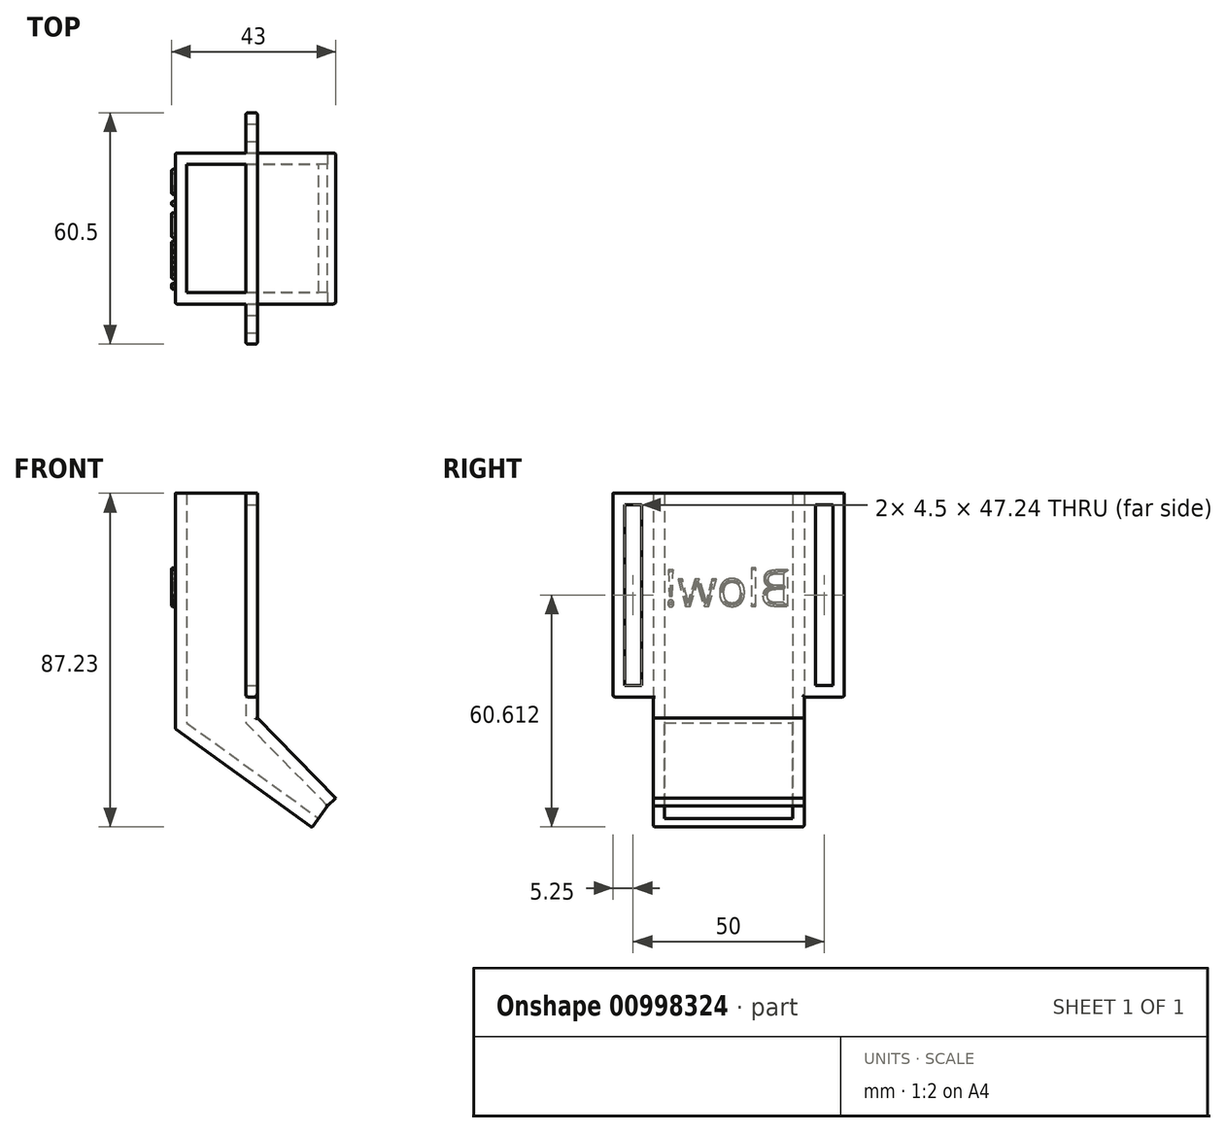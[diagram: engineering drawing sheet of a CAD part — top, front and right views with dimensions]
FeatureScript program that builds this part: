
annotation { "Feature Type Name" : "Feature", "Feature Type Description" : "" }
export const myFeature = defineFeature(function(context is Context, id is Id, definition is map)
    precondition{}
    {
        {
            assignVariable(context, id + "F0", {"name" : "lenght", "anyValue" : 33.5});
        }
        {
            assignVariable(context, id + "F1", {"name" : "WallThicness", "anyValue" : 3});
        }
        {
            assignVariable(context, id + "F2", {"name" : "screwdiam", "anyValue" : 4.5});
        }
        {
            var Q0;
            Q0=qCreatedBy(makeId("Front.planeOp"),FACE);
            var sketch = newSketch(context, id + "F3", { "sketchPlane" : qUnion([Q0])});
            skLineSegment(sketch, "E0.bottom", {"start": v(-2.56, 51.75) * mm, "end": v(12.94, 51.75) * mm});
            skLineSegment(sketch, "E0.left", {"start": v(-2.56, 51.75) * mm, "end": v(-2.56, -8.25) * mm});
            skLineSegment(sketch, "E0.right", {"start": v(12.94, 51.75) * mm, "end": v(12.94, -8.25) * mm});
            skLineSegment(sketch, "E1", {"start": v(-2.56, -8.25) * mm, "end": v(31.95, -33.25) * mm});
            skLineSegment(sketch, "E2", {"start": v(31.95, -33.25) * mm, "end": v(34.3, -30) * mm});
            skLineSegment(sketch, "E3", {"start": v(34.3, -30) * mm, "end": v(12.94, -8.25) * mm});
            skLineSegment(sketch, "E4.0", {"start": v(36.44, -27.9) * mm, "end": v(15.94, -7.02) * mm});
            skLineSegment(sketch, "E4.1", {"start": v(15.94, 51.75) * mm, "end": v(15.94, -7.02) * mm});
            skLineSegment(sketch, "E5.0", {"start": v(-5.56, -9.78) * mm, "end": v(30.19, -35.68) * mm});
            skLineSegment(sketch, "E5.1", {"start": v(-5.56, 51.75) * mm, "end": v(-5.56, -9.78) * mm});
            skLineSegment(sketch, "E6", {"start": v(12.94, 51.75) * mm, "end": v(15.94, 51.75) * mm});
            skLineSegment(sketch, "E7", {"start": v(-5.56, 51.75) * mm, "end": v(-2.56, 51.75) * mm});
            skLineSegment(sketch, "E8", {"start": v(31.95, -33.25) * mm, "end": v(30.19, -35.68) * mm});
            skLineSegment(sketch, "E9", {"start": v(36.44, -27.9) * mm, "end": v(34.3, -30) * mm});
            skSolve(sketch);
        }
        {
            var Q0;
            Q0=makeQuery(id+"F3.imprint","IMPRINT",FACE,{"disambiguationData":[TD([[makeQuery(id+"F3.imprint","IMPRINT",EDGE,{"derivedFrom":sQuery(id+"F3.wireOp",EDGE,"E0.right")}),1.0]])]});
            var Q1;
            Q1=makeQuery(id+"F3.imprint","IMPRINT",FACE,{"disambiguationData":[TD([[makeQuery(id+"F3.imprint","IMPRINT",EDGE,{"derivedFrom":sQuery(id+"F3.wireOp",EDGE,"E0.left")}),-1.0]])]});
            extrude(context, id + "F4", {"entities" : qUnion([Q0, Q1]), "endBound" : BoundingType.SYMMETRIC, "depth" : (getVariable(context, 'lenght')) * mm, "offsetDistance" : 25 * mm});
        }
        {
            var Q0;
            Q0 = qSketchRegion(id + "F3", true);
            extrude(context, id + "F5", {"entities" : qUnion([Q0]), "endBound" : BoundingType.SYMMETRIC, "oppositeDirection" : true, "depth" : (getVariable(context, 'WallThicness')) * mm, "offsetDistance" : 25 * mm});
        }
        {
            var Q0;
            Q0=makeQuery(id+"F5.opExtrude","SWEPT_BODY",BODY,{"disambiguationData":[OSD([sQuery(id+"F3.wireOp",EDGE,"E0.bottom"),sQuery(id+"F3.wireOp",EDGE,"E2"),sQuery(id+"F3.wireOp",EDGE,"E4.0"),sQuery(id+"F3.wireOp",EDGE,"E4.1"),sQuery(id+"F3.wireOp",EDGE,"E5.0"),sQuery(id+"F3.wireOp",EDGE,"E5.1"),sQuery(id+"F3.wireOp",EDGE,"E6"),sQuery(id+"F3.wireOp",EDGE,"E7"),sQuery(id+"F3.wireOp",EDGE,"E8"),sQuery(id+"F3.wireOp",EDGE,"E9")])]});
            var Q1;
            Q1=makeQuery(id+"F4.opExtrude","SWEPT_EDGE",EDGE,{"disambiguationData":[OSD([sQuery(id+"F3.wireOp",EDGE,"E5.1"),sQuery(id+"F3.wireOp",EDGE,"E7")])]});
            transform(context, id + "F6", {"entities" : qUnion([Q0]), "transformType" : TransformType.TRANSLATION_DISTANCE, "transformDirection" : qUnion([Q1]), "distance" : ((getVariable(context, 'lenght') + getVariable(context, 'WallThicness')) / 2) * mm, "oppositeDirection" : true, "makeCopy" : true});
        }
        {
            var Q0;
            Q0=makeQuery(id+"F5.opExtrude","SWEPT_BODY",BODY,{"disambiguationData":[OSD([sQuery(id+"F3.wireOp",EDGE,"E0.bottom"),sQuery(id+"F3.wireOp",EDGE,"E2"),sQuery(id+"F3.wireOp",EDGE,"E4.0"),sQuery(id+"F3.wireOp",EDGE,"E4.1"),sQuery(id+"F3.wireOp",EDGE,"E5.0"),sQuery(id+"F3.wireOp",EDGE,"E5.1"),sQuery(id+"F3.wireOp",EDGE,"E6"),sQuery(id+"F3.wireOp",EDGE,"E7"),sQuery(id+"F3.wireOp",EDGE,"E8"),sQuery(id+"F3.wireOp",EDGE,"E9")])]});
            var Q1;
            Q1=makeQuery(id+"F4.opExtrude","SWEPT_EDGE",EDGE,{"disambiguationData":[OSD([sQuery(id+"F3.wireOp",EDGE,"E5.1"),sQuery(id+"F3.wireOp",EDGE,"E7")])]});
            transform(context, id + "F7", {"entities" : qUnion([Q0]), "transformType" : TransformType.TRANSLATION_DISTANCE, "transformDirection" : qUnion([Q1]), "distance" : ((getVariable(context, 'lenght') + getVariable(context, 'WallThicness')) / 2) * mm, "makeCopy" : false});
        }
        {
            var Q0;
            Q0=makeQuery(id+"F5.opExtrude","CAP_FACE",FACE,{"disambiguationData":[OSD([sQuery(id+"F3.wireOp",EDGE,"E0.bottom"),sQuery(id+"F3.wireOp",EDGE,"E2"),sQuery(id+"F3.wireOp",EDGE,"E4.0"),sQuery(id+"F3.wireOp",EDGE,"E4.1"),sQuery(id+"F3.wireOp",EDGE,"E5.0"),sQuery(id+"F3.wireOp",EDGE,"E5.1"),sQuery(id+"F3.wireOp",EDGE,"E6"),sQuery(id+"F3.wireOp",EDGE,"E7"),sQuery(id+"F3.wireOp",EDGE,"E8"),sQuery(id+"F3.wireOp",EDGE,"E9")])],"isStart":true});
            var sketch = newSketch(context, id + "F8", { "sketchPlane" : qUnion([Q0])});
            skLineSegment(sketch, "E10.bottom", {"start": v(15.94, 51.75) * mm, "end": v(12.94, 51.75) * mm});
            skLineSegment(sketch, "E10.top", {"start": v(15.94, -1.49) * mm, "end": v(12.94, -1.49) * mm});
            skLineSegment(sketch, "E10.left", {"start": v(15.94, 51.75) * mm, "end": v(15.94, -1.49) * mm});
            skLineSegment(sketch, "E10.right", {"start": v(12.94, 51.75) * mm, "end": v(12.94, -1.49) * mm});
            skSolve(sketch);
        }
        {
            var Q0;
            Q0 = qSketchRegion(id + "F8", true);
            extrude(context, id + "F9", {"entities" : qUnion([Q0]), "oppositeDirection" : true, "depth" : (3 * getVariable(context, 'WallThicness') + getVariable(context, 'screwdiam')) * mm, "offsetDistance" : 25 * mm});
        }
        {
            var Q0;
            Q0=makeQuery(id+"F9.opExtrude","SWEPT_FACE",FACE,{"disambiguationData":[OSD([sQuery(id+"F8.wireOp",EDGE,"E10.left")])]});
            var sketch = newSketch(context, id + "F10", { "sketchPlane" : qUnion([Q0])});
            skLineSegment(sketch, "E11.bottom", {"start": v(27.25, 48.75) * mm, "end": v(22.75, 48.75) * mm});
            skLineSegment(sketch, "E11.top", {"start": v(27.25, 1.51) * mm, "end": v(22.75, 1.51) * mm});
            skLineSegment(sketch, "E11.left", {"start": v(27.25, 48.75) * mm, "end": v(27.25, 1.51) * mm});
            skLineSegment(sketch, "E11.right", {"start": v(22.75, 48.75) * mm, "end": v(22.75, 1.51) * mm});
            skSolve(sketch);
        }
        {
            var Q0;
            Q0=makeQuery(id+"F10.imprint","IMPRINT",FACE,{"disambiguationData":[TD([[makeQuery(id+"F10.imprint","IMPRINT",EDGE,{"derivedFrom":sQuery(id+"F10.wireOp",EDGE,"E11.bottom")}),1.0]])]});
            extrude(context, id + "F11", {"entities" : qUnion([Q0]), "operationType" : NewBodyOperationType.REMOVE, "endBound" : BoundingType.THROUGH_ALL, "oppositeDirection" : true, "depth" : 25 * mm, "offsetDistance" : 25 * mm});
        }
        {
            var Q0;
            Q0=makeQuery(id+"F9.opExtrude","SWEPT_BODY",BODY,{"disambiguationData":[OSD([sQuery(id+"F8.wireOp",EDGE,"E10.bottom"),sQuery(id+"F8.wireOp",EDGE,"E10.top"),sQuery(id+"F8.wireOp",EDGE,"E10.left"),sQuery(id+"F8.wireOp",EDGE,"E10.right")])]});
            var Q1;
            Q1=qCreatedBy(makeId("Front.planeOp"),FACE);
            mirror(context, id + "F12", {"operationType" : NewBodyOperationType.ADD, "entities" : qUnion([Q0]), "mirrorPlane" : qUnion([Q1])});
        }
        {
            var Q0;
            Q0=makeQuery(id+"F4.opExtrude","SWEPT_BODY",BODY,{"disambiguationData":[OSD([sQuery(id+"F3.wireOp",EDGE,"E0.left"),sQuery(id+"F3.wireOp",EDGE,"E1"),sQuery(id+"F3.wireOp",EDGE,"E5.0"),sQuery(id+"F3.wireOp",EDGE,"E5.1"),sQuery(id+"F3.wireOp",EDGE,"E7"),sQuery(id+"F3.wireOp",EDGE,"E8")])]});
            var Q1;
            Q1=makeQuery(id+"F4.opExtrude","SWEPT_BODY",BODY,{"disambiguationData":[OSD([sQuery(id+"F3.wireOp",EDGE,"E0.right"),sQuery(id+"F3.wireOp",EDGE,"E3"),sQuery(id+"F3.wireOp",EDGE,"E4.0"),sQuery(id+"F3.wireOp",EDGE,"E4.1"),sQuery(id+"F3.wireOp",EDGE,"E6"),sQuery(id+"F3.wireOp",EDGE,"E9")])]});
            var Q2;
            Q2=makeQuery(id+"F5.opExtrude","SWEPT_BODY",BODY,{"disambiguationData":[OSD([sQuery(id+"F3.wireOp",EDGE,"E0.bottom"),sQuery(id+"F3.wireOp",EDGE,"E2"),sQuery(id+"F3.wireOp",EDGE,"E4.0"),sQuery(id+"F3.wireOp",EDGE,"E4.1"),sQuery(id+"F3.wireOp",EDGE,"E5.0"),sQuery(id+"F3.wireOp",EDGE,"E5.1"),sQuery(id+"F3.wireOp",EDGE,"E6"),sQuery(id+"F3.wireOp",EDGE,"E7"),sQuery(id+"F3.wireOp",EDGE,"E8"),sQuery(id+"F3.wireOp",EDGE,"E9")])]});
            var Q3;
            Q3=makeQuery(id+"F6.opPattern","COPY",BODY,{"derivedFrom":makeQuery(id+"F5.opExtrude","SWEPT_BODY",BODY,{"disambiguationData":[OSD([sQuery(id+"F3.wireOp",EDGE,"E0.bottom"),sQuery(id+"F3.wireOp",EDGE,"E2"),sQuery(id+"F3.wireOp",EDGE,"E4.0"),sQuery(id+"F3.wireOp",EDGE,"E4.1"),sQuery(id+"F3.wireOp",EDGE,"E5.0"),sQuery(id+"F3.wireOp",EDGE,"E5.1"),sQuery(id+"F3.wireOp",EDGE,"E6"),sQuery(id+"F3.wireOp",EDGE,"E7"),sQuery(id+"F3.wireOp",EDGE,"E8"),sQuery(id+"F3.wireOp",EDGE,"E9")])]}),"instanceName":"1"});
            var Q4;
            Q4=makeQuery(id+"F9.opExtrude","SWEPT_BODY",BODY,{"disambiguationData":[OSD([sQuery(id+"F8.wireOp",EDGE,"E10.bottom"),sQuery(id+"F8.wireOp",EDGE,"E10.top"),sQuery(id+"F8.wireOp",EDGE,"E10.left"),sQuery(id+"F8.wireOp",EDGE,"E10.right")])]});
            var Q5;
            Q5=makeQuery(id+"F12.opPattern","COPY",BODY,{"derivedFrom":makeQuery(id+"F9.opExtrude","SWEPT_BODY",BODY,{"disambiguationData":[OSD([sQuery(id+"F8.wireOp",EDGE,"E10.bottom"),sQuery(id+"F8.wireOp",EDGE,"E10.top"),sQuery(id+"F8.wireOp",EDGE,"E10.left"),sQuery(id+"F8.wireOp",EDGE,"E10.right")])]}),"instanceName":"1"});
            booleanBodies(context, id + "F13", {"operationType" : BooleanOperationType.UNION, "tools" : qUnion([Q0, Q1, Q2, Q3, Q4, Q5])});
        }
        {
            var Q0;
            {var subQ0=sQuery(id+"F3.wireOp",EDGE,"E9");var subQ1=sQuery(id+"F3.wireOp",EDGE,"E4.0");var subQ2=makeQuery(id+"F5.opExtrude","SWEPT_EDGE",EDGE,{"disambiguationData":[OSD([subQ1,subQ0])]});Q0=makeQuery(id+"F13.opBoolean","MERGE",EDGE,{"derivedFrom":[makeQuery(id+"F4.opExtrude","SWEPT_EDGE",EDGE,{"disambiguationData":[OSD([subQ1,subQ0])]}),subQ2,makeQuery(id+"F6.opPattern","COPY",EDGE,{"derivedFrom":subQ2,"instanceName":"1"})]});}
            var Q1;
            Q1=makeQuery(id+"F5.opExtrude","CAP_EDGE",EDGE,{"disambiguationData":[OSD([sQuery(id+"F3.wireOp",EDGE,"E4.0")])],"isStart":false});
            var Q2;
            Q2=makeQuery(id+"F5.opExtrude","CAP_EDGE",EDGE,{"disambiguationData":[OSD([sQuery(id+"F3.wireOp",EDGE,"E2"),sQuery(id+"F3.wireOp",EDGE,"E8")])],"isStart":false});
            var Q3;
            Q3=makeQuery(id+"F5.opExtrude","CAP_EDGE",EDGE,{"disambiguationData":[OSD([sQuery(id+"F3.wireOp",EDGE,"E9")])],"isStart":false});
            var Q4;
            {var subQ0=sQuery(id+"F3.wireOp",EDGE,"E8");var subQ1=sQuery(id+"F3.wireOp",EDGE,"E5.0");var subQ2=makeQuery(id+"F5.opExtrude","SWEPT_EDGE",EDGE,{"disambiguationData":[OSD([subQ1,subQ0])]});Q4=makeQuery(id+"F13.opBoolean","MERGE",EDGE,{"derivedFrom":[makeQuery(id+"F4.opExtrude","SWEPT_EDGE",EDGE,{"disambiguationData":[OSD([subQ1,subQ0])]}),subQ2,makeQuery(id+"F6.opPattern","COPY",EDGE,{"derivedFrom":subQ2,"instanceName":"1"})]});}
            var Q5;
            Q5=makeQuery(id+"F6.opPattern","COPY",EDGE,{"derivedFrom":makeQuery(id+"F5.opExtrude","CAP_EDGE",EDGE,{"disambiguationData":[OSD([sQuery(id+"F3.wireOp",EDGE,"E9")])],"isStart":true}),"instanceName":"1"});
            var Q6;
            Q6=makeQuery(id+"F6.opPattern","COPY",EDGE,{"derivedFrom":makeQuery(id+"F5.opExtrude","CAP_EDGE",EDGE,{"disambiguationData":[OSD([sQuery(id+"F3.wireOp",EDGE,"E2"),sQuery(id+"F3.wireOp",EDGE,"E8")])],"isStart":true}),"instanceName":"1"});
            var Q7;
            Q7=makeQuery(id+"F6.opPattern","COPY",EDGE,{"derivedFrom":makeQuery(id+"F5.opExtrude","CAP_EDGE",EDGE,{"disambiguationData":[OSD([sQuery(id+"F3.wireOp",EDGE,"E4.0")])],"isStart":true}),"instanceName":"1"});
            var Q8;
            Q8=makeQuery(id+"F5.opExtrude","CAP_EDGE",EDGE,{"disambiguationData":[OSD([sQuery(id+"F3.wireOp",EDGE,"E4.1")])],"isStart":false});
            var Q9;
            Q9=makeQuery(id+"F9.opExtrude","SWEPT_EDGE",EDGE,{"disambiguationData":[OSD([sQuery(id+"F3.wireOp",EDGE,"E4.1"),sQuery(id+"F8.wireOp",EDGE,"E10.top"),sQuery(id+"F8.wireOp",EDGE,"E10.left")])]});
            var Q10;
            Q10=makeQuery(id+"F9.opExtrude","CAP_EDGE",EDGE,{"disambiguationData":[OSD([sQuery(id+"F8.wireOp",EDGE,"E10.left")])],"isStart":false});
            var Q11;
            Q11=makeQuery(id+"F5.opExtrude","CAP_EDGE",EDGE,{"disambiguationData":[OSD([sQuery(id+"F3.wireOp",EDGE,"E5.0")])],"isStart":false});
            var Q12;
            Q12=makeQuery(id+"F5.opExtrude","CAP_EDGE",EDGE,{"disambiguationData":[OSD([sQuery(id+"F3.wireOp",EDGE,"E5.1")])],"isStart":false});
            var Q13;
            Q13=makeQuery(id+"F9.opExtrude","SWEPT_EDGE",EDGE,{"disambiguationData":[OSD([sQuery(id+"F8.wireOp",EDGE,"E10.top"),sQuery(id+"F8.wireOp",EDGE,"E10.right")])]});
            var Q14;
            Q14=makeQuery(id+"F9.opExtrude","CAP_EDGE",EDGE,{"disambiguationData":[OSD([sQuery(id+"F8.wireOp",EDGE,"E10.top")])],"isStart":false});
            var Q15;
            {var subQ0=sQuery(id+"F3.wireOp",EDGE,"E5.1");var subQ1=sQuery(id+"F3.wireOp",EDGE,"E5.0");var subQ2=makeQuery(id+"F5.opExtrude","SWEPT_EDGE",EDGE,{"disambiguationData":[OSD([subQ1,subQ0])]});Q15=makeQuery(id+"F13.opBoolean","MERGE",EDGE,{"derivedFrom":[makeQuery(id+"F4.opExtrude","SWEPT_EDGE",EDGE,{"disambiguationData":[OSD([subQ1,subQ0])]}),subQ2,makeQuery(id+"F6.opPattern","COPY",EDGE,{"derivedFrom":subQ2,"instanceName":"1"})]});}
            var Q16;
            Q16=makeQuery(id+"F6.opPattern","COPY",EDGE,{"derivedFrom":makeQuery(id+"F5.opExtrude","CAP_EDGE",EDGE,{"disambiguationData":[OSD([sQuery(id+"F3.wireOp",EDGE,"E5.1")])],"isStart":true}),"instanceName":"1"});
            var Q17;
            Q17=makeQuery(id+"F6.opPattern","COPY",EDGE,{"derivedFrom":makeQuery(id+"F5.opExtrude","CAP_EDGE",EDGE,{"disambiguationData":[OSD([sQuery(id+"F3.wireOp",EDGE,"E4.1")])],"isStart":true}),"instanceName":"1"});
            var Q18;
            Q18=makeQuery(id+"F12.opPattern","COPY",EDGE,{"derivedFrom":makeQuery(id+"F9.opExtrude","SWEPT_EDGE",EDGE,{"disambiguationData":[OSD([sQuery(id+"F8.wireOp",EDGE,"E10.top"),sQuery(id+"F8.wireOp",EDGE,"E10.right")])]}),"instanceName":"1"});
            var Q19;
            Q19=makeQuery(id+"F12.opPattern","COPY",EDGE,{"derivedFrom":makeQuery(id+"F9.opExtrude","CAP_EDGE",EDGE,{"disambiguationData":[OSD([sQuery(id+"F8.wireOp",EDGE,"E10.right")])],"isStart":false}),"instanceName":"1"});
            var Q20;
            Q20=makeQuery(id+"F12.opPattern","COPY",EDGE,{"derivedFrom":makeQuery(id+"F9.opExtrude","CAP_EDGE",EDGE,{"disambiguationData":[OSD([sQuery(id+"F8.wireOp",EDGE,"E10.top")])],"isStart":false}),"instanceName":"1"});
            var Q21;
            Q21=makeQuery(id+"F12.opPattern","COPY",EDGE,{"derivedFrom":makeQuery(id+"F9.opExtrude","CAP_EDGE",EDGE,{"disambiguationData":[OSD([sQuery(id+"F8.wireOp",EDGE,"E10.left")])],"isStart":false}),"instanceName":"1"});
            var Q22;
            Q22=makeQuery(id+"F9.opExtrude","CAP_EDGE",EDGE,{"disambiguationData":[OSD([sQuery(id+"F8.wireOp",EDGE,"E10.right")])],"isStart":false});
            var Q23;
            Q23=makeQuery(id+"F6.opPattern","COPY",EDGE,{"derivedFrom":makeQuery(id+"F5.opExtrude","CAP_EDGE",EDGE,{"disambiguationData":[OSD([sQuery(id+"F3.wireOp",EDGE,"E5.0")])],"isStart":true}),"instanceName":"1"});
            fillet(context, id + "F14", {"entities" : qUnion([Q0, Q1, Q2, Q3, Q4, Q5, Q6, Q7, Q8, Q9, Q10, Q11, Q12, Q13, Q14, Q15, Q16, Q17, Q18, Q19, Q20, Q21, Q22, Q23]), "radius" : 0.5 * mm, "tangentPropagation" : true, "allowEdgeOverflow" : false});
        }
        {
            var Q0;
            {var subQ0=sQuery(id+"F3.wireOp",EDGE,"E5.1");var subQ1=makeQuery(id+"F5.opExtrude","SWEPT_FACE",FACE,{"disambiguationData":[OSD([subQ0])]});Q0=makeQuery(id+"F13.opBoolean","MERGE",FACE,{"derivedFrom":[makeQuery(id+"F4.opExtrude","SWEPT_FACE",FACE,{"disambiguationData":[OSD([subQ0])]}),subQ1,makeQuery(id+"F6.opPattern","COPY",FACE,{"derivedFrom":subQ1,"instanceName":"1"})]});}
            var sketch = newSketch(context, id + "F15", { "sketchPlane" : qUnion([Q0])});
            skText(sketch, "E12", { "text": "Blow!", "fontName": "OpenSans-Regular.ttf"});
            skLineSegment(sketch, "E13", {"start": v(16.75, 37) * mm, "end": v(19.25, 37) * mm, "construction": true});
            skLineSegment(sketch, "E14", {"start": v(-16.75, 10.2) * mm, "end": v(-19.25, 10.2) * mm, "construction": true});
            const initialGuessF15  = {"E12": [-0.01675, 0.02225, 1, 0, 0.0095]};
            skSetInitialGuess(sketch, initialGuessF15);
            skSolve(sketch);
        }
        {
            var Q0;
            Q0=makeQuery(id+"F15.imprint","IMPRINT",FACE,{"disambiguationData":[TD([[makeQuery(id+"F15.imprint","IMPRINT",EDGE,{"derivedFrom":sQuery(id+"F15.wireOp",EDGE,"E12.sketch_text.stroke-73")}),-1.0]])]});
            var Q1;
            Q1=makeQuery(id+"F15.imprint","IMPRINT",FACE,{"disambiguationData":[TD([[makeQuery(id+"F15.imprint","IMPRINT",EDGE,{"derivedFrom":sQuery(id+"F15.wireOp",EDGE,"E12.sketch_text.stroke-69")}),-1.0]])]});
            var Q2;
            Q2=makeQuery(id+"F15.imprint","IMPRINT",FACE,{"disambiguationData":[TD([[makeQuery(id+"F15.imprint","IMPRINT",EDGE,{"derivedFrom":sQuery(id+"F15.wireOp",EDGE,"E12.sketch_text.stroke-46")}),-1.0]])]});
            var Q3;
            Q3=makeQuery(id+"F15.imprint","IMPRINT",FACE,{"disambiguationData":[TD([[makeQuery(id+"F15.imprint","IMPRINT",EDGE,{"derivedFrom":sQuery(id+"F15.wireOp",EDGE,"E12.sketch_text.stroke-29")}),-1.0]])]});
            var Q4;
            Q4=makeQuery(id+"F15.imprint","IMPRINT",FACE,{"disambiguationData":[TD([[makeQuery(id+"F15.imprint","IMPRINT",EDGE,{"derivedFrom":sQuery(id+"F15.wireOp",EDGE,"E12.sketch_text.stroke-25")}),-1.0]])]});
            var Q5;
            Q5=makeQuery(id+"F15.imprint","IMPRINT",FACE,{"disambiguationData":[TD([[makeQuery(id+"F15.imprint","IMPRINT",EDGE,{"derivedFrom":sQuery(id+"F15.wireOp",EDGE,"E12.sketch_text.stroke-0")}),-1.0]])]});
            extrude(context, id + "F16", {"entities" : qUnion([Q0, Q1, Q2, Q3, Q4, Q5]), "operationType" : NewBodyOperationType.ADD, "depth" : 1 * mm, "offsetDistance" : 25 * mm});
        }
        {
            var Q0;
            Q0=makeQuery(id+"F16.opExtrude","CAP_FACE",FACE,{"disambiguationData":[OSD([sQuery(id+"F15.wireOp",EDGE,"E12.sketch_text.stroke-0"),sQuery(id+"F15.wireOp",EDGE,"E12.sketch_text.stroke-1"),sQuery(id+"F15.wireOp",EDGE,"E12.sketch_text.stroke-2"),sQuery(id+"F15.wireOp",EDGE,"E12.sketch_text.stroke-3"),sQuery(id+"F15.wireOp",EDGE,"E12.sketch_text.stroke-4"),sQuery(id+"F15.wireOp",EDGE,"E12.sketch_text.stroke-5"),sQuery(id+"F15.wireOp",EDGE,"E12.sketch_text.stroke-6"),sQuery(id+"F15.wireOp",EDGE,"E12.sketch_text.stroke-7"),sQuery(id+"F15.wireOp",EDGE,"E12.sketch_text.stroke-8"),sQuery(id+"F15.wireOp",EDGE,"E12.sketch_text.stroke-9"),sQuery(id+"F15.wireOp",EDGE,"E12.sketch_text.stroke-10"),sQuery(id+"F15.wireOp",EDGE,"E12.sketch_text.stroke-11"),sQuery(id+"F15.wireOp",EDGE,"E12.sketch_text.stroke-12"),sQuery(id+"F15.wireOp",EDGE,"E12.sketch_text.stroke-13"),sQuery(id+"F15.wireOp",EDGE,"E12.sketch_text.stroke-14"),sQuery(id+"F15.wireOp",EDGE,"E12.sketch_text.stroke-15"),sQuery(id+"F15.wireOp",EDGE,"E12.sketch_text.stroke-16"),sQuery(id+"F15.wireOp",EDGE,"E12.sketch_text.stroke-17"),sQuery(id+"F15.wireOp",EDGE,"E12.sketch_text.stroke-18"),sQuery(id+"F15.wireOp",EDGE,"E12.sketch_text.stroke-19"),sQuery(id+"F15.wireOp",EDGE,"E12.sketch_text.stroke-20"),sQuery(id+"F15.wireOp",EDGE,"E12.sketch_text.stroke-21"),sQuery(id+"F15.wireOp",EDGE,"E12.sketch_text.stroke-22"),sQuery(id+"F15.wireOp",EDGE,"E12.sketch_text.stroke-23"),sQuery(id+"F15.wireOp",EDGE,"E12.sketch_text.stroke-24")])],"isStart":false});
            var Q1;
            Q1=makeQuery(id+"F16.opExtrude","CAP_FACE",FACE,{"disambiguationData":[OSD([sQuery(id+"F15.wireOp",EDGE,"E12.sketch_text.stroke-25"),sQuery(id+"F15.wireOp",EDGE,"E12.sketch_text.stroke-26"),sQuery(id+"F15.wireOp",EDGE,"E12.sketch_text.stroke-27"),sQuery(id+"F15.wireOp",EDGE,"E12.sketch_text.stroke-28")])],"isStart":false});
            var Q2;
            Q2=makeQuery(id+"F16.opExtrude","CAP_FACE",FACE,{"disambiguationData":[OSD([sQuery(id+"F15.wireOp",EDGE,"E12.sketch_text.stroke-29"),sQuery(id+"F15.wireOp",EDGE,"E12.sketch_text.stroke-30"),sQuery(id+"F15.wireOp",EDGE,"E12.sketch_text.stroke-31"),sQuery(id+"F15.wireOp",EDGE,"E12.sketch_text.stroke-32"),sQuery(id+"F15.wireOp",EDGE,"E12.sketch_text.stroke-33"),sQuery(id+"F15.wireOp",EDGE,"E12.sketch_text.stroke-34"),sQuery(id+"F15.wireOp",EDGE,"E12.sketch_text.stroke-35"),sQuery(id+"F15.wireOp",EDGE,"E12.sketch_text.stroke-36"),sQuery(id+"F15.wireOp",EDGE,"E12.sketch_text.stroke-37"),sQuery(id+"F15.wireOp",EDGE,"E12.sketch_text.stroke-38"),sQuery(id+"F15.wireOp",EDGE,"E12.sketch_text.stroke-39"),sQuery(id+"F15.wireOp",EDGE,"E12.sketch_text.stroke-40"),sQuery(id+"F15.wireOp",EDGE,"E12.sketch_text.stroke-41"),sQuery(id+"F15.wireOp",EDGE,"E12.sketch_text.stroke-42"),sQuery(id+"F15.wireOp",EDGE,"E12.sketch_text.stroke-43"),sQuery(id+"F15.wireOp",EDGE,"E12.sketch_text.stroke-44"),sQuery(id+"F15.wireOp",EDGE,"E12.sketch_text.stroke-45")])],"isStart":false});
            var Q3;
            Q3=makeQuery(id+"F16.opExtrude","CAP_FACE",FACE,{"disambiguationData":[OSD([sQuery(id+"F15.wireOp",EDGE,"E12.sketch_text.stroke-46"),sQuery(id+"F15.wireOp",EDGE,"E12.sketch_text.stroke-47"),sQuery(id+"F15.wireOp",EDGE,"E12.sketch_text.stroke-48"),sQuery(id+"F15.wireOp",EDGE,"E12.sketch_text.stroke-49"),sQuery(id+"F15.wireOp",EDGE,"E12.sketch_text.stroke-50"),sQuery(id+"F15.wireOp",EDGE,"E12.sketch_text.stroke-51"),sQuery(id+"F15.wireOp",EDGE,"E12.sketch_text.stroke-52"),sQuery(id+"F15.wireOp",EDGE,"E12.sketch_text.stroke-53"),sQuery(id+"F15.wireOp",EDGE,"E12.sketch_text.stroke-54"),sQuery(id+"F15.wireOp",EDGE,"E12.sketch_text.stroke-55"),sQuery(id+"F15.wireOp",EDGE,"E12.sketch_text.stroke-56"),sQuery(id+"F15.wireOp",EDGE,"E12.sketch_text.stroke-57"),sQuery(id+"F15.wireOp",EDGE,"E12.sketch_text.stroke-58"),sQuery(id+"F15.wireOp",EDGE,"E12.sketch_text.stroke-59"),sQuery(id+"F15.wireOp",EDGE,"E12.sketch_text.stroke-60"),sQuery(id+"F15.wireOp",EDGE,"E12.sketch_text.stroke-61"),sQuery(id+"F15.wireOp",EDGE,"E12.sketch_text.stroke-62"),sQuery(id+"F15.wireOp",EDGE,"E12.sketch_text.stroke-63"),sQuery(id+"F15.wireOp",EDGE,"E12.sketch_text.stroke-64"),sQuery(id+"F15.wireOp",EDGE,"E12.sketch_text.stroke-65"),sQuery(id+"F15.wireOp",EDGE,"E12.sketch_text.stroke-66"),sQuery(id+"F15.wireOp",EDGE,"E12.sketch_text.stroke-67"),sQuery(id+"F15.wireOp",EDGE,"E12.sketch_text.stroke-68")])],"isStart":false});
            var Q4;
            Q4=makeQuery(id+"F16.opExtrude","CAP_FACE",FACE,{"disambiguationData":[OSD([sQuery(id+"F15.wireOp",EDGE,"E12.sketch_text.stroke-69"),sQuery(id+"F15.wireOp",EDGE,"E12.sketch_text.stroke-70"),sQuery(id+"F15.wireOp",EDGE,"E12.sketch_text.stroke-71"),sQuery(id+"F15.wireOp",EDGE,"E12.sketch_text.stroke-72")])],"isStart":false});
            var Q5;
            Q5=makeQuery(id+"F16.opExtrude","CAP_FACE",FACE,{"disambiguationData":[OSD([sQuery(id+"F15.wireOp",EDGE,"E12.sketch_text.stroke-73"),sQuery(id+"F15.wireOp",EDGE,"E12.sketch_text.stroke-74"),sQuery(id+"F15.wireOp",EDGE,"E12.sketch_text.stroke-75"),sQuery(id+"F15.wireOp",EDGE,"E12.sketch_text.stroke-76"),sQuery(id+"F15.wireOp",EDGE,"E12.sketch_text.stroke-77"),sQuery(id+"F15.wireOp",EDGE,"E12.sketch_text.stroke-78"),sQuery(id+"F15.wireOp",EDGE,"E12.sketch_text.stroke-79")])],"isStart":false});
            fillet(context, id + "F17", {"entities" : qUnion([Q0, Q1, Q2, Q3, Q4, Q5]), "radius" : 0.5 * mm, "tangentPropagation" : true, "allowEdgeOverflow" : false});
        }
    });
